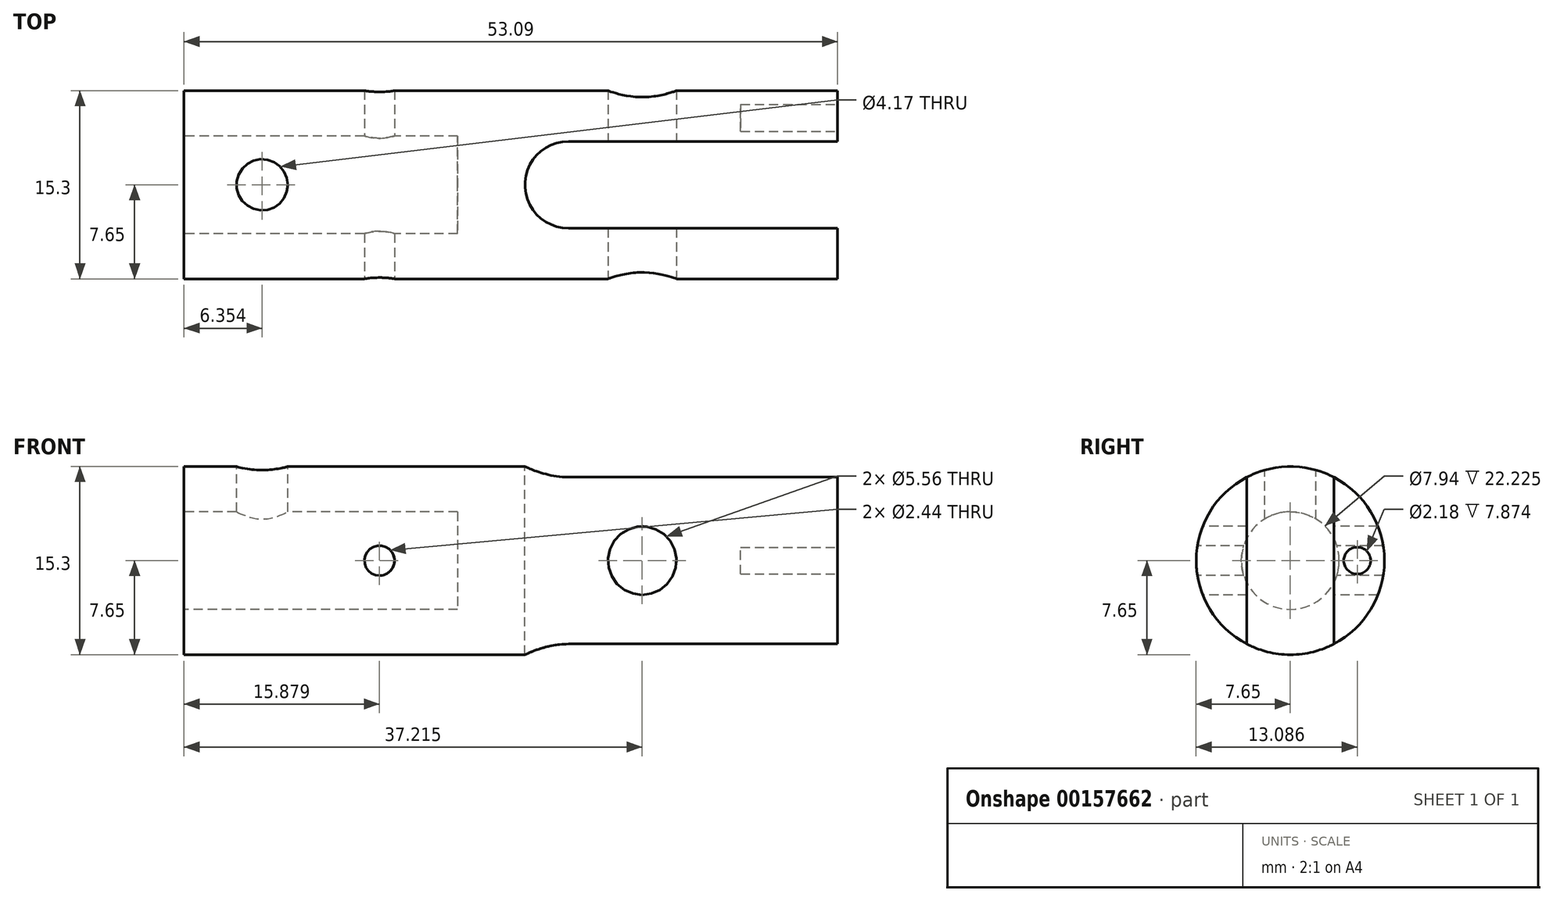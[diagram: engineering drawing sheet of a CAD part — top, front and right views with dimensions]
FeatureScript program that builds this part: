
annotation { "Feature Type Name" : "Feature", "Feature Type Description" : "" }
export const myFeature = defineFeature(function(context is Context, id is Id, definition is map)
    precondition{}
    {
        {
            var Q0;
            Q0=qCreatedBy(makeId("Right.planeOp"),FACE);
            var sketch = newSketch(context, id + "F0", { "sketchPlane" : qUnion([Q0])});
            skCircle(sketch, "E0", {"center": v(0, 0) * mm, "radius": 7.65 * mm});
            skSolve(sketch);
        }
        {
            var Q0;
            Q0=makeQuery(id+"F0.imprint","IMPRINT",FACE,{"disambiguationData":[TD([[makeQuery(id+"F0.imprint","IMPRINT",EDGE,{"derivedFrom":sQuery(id+"F0.wireOp",EDGE,"E0")}),1.0]])]});
            extrude(context, id + "F1", {"entities" : qUnion([Q0]), "oppositeDirection" : true, "depth" : 53.1 * mm});
        }
        {
            var Q0;
            Q0=qCreatedBy(makeId("Top.planeOp"),FACE);
            cPlane(context, id + "F2", {"entities" : qUnion([Q0]), "cplaneType" : CPlaneType.OFFSET, "offset" : 7.87 * mm, "width" : 152.4 * mm, "height" : 152.4 * mm});
        }
        {
            var Q0;
            Q0=qCreatedBy(id+"F2.planeOp",FACE);
            var sketch = newSketch(context, id + "F3", { "sketchPlane" : qUnion([Q0])});
            skLineSegment(sketch, "E1.bottom", {"start": v(-21.87, 3.53) * mm, "end": v(25.4, 3.53) * mm});
            skLineSegment(sketch, "E1.top", {"start": v(-21.87, -3.53) * mm, "end": v(25.4, -3.53) * mm});
            skLineSegment(sketch, "E1.left", {"start": v(-25.4, 0) * mm, "end": v(-25.4, 0) * mm});
            skLineSegment(sketch, "E1.right", {"start": v(25.4, 3.53) * mm, "end": v(25.4, -3.53) * mm});
            skPoint(sketch, "E1.middle", {"position": v(0, 0) * mm});
            skPoint(sketch, "E2.visualSharp", {"position": v(-25.4, 3.53) * mm});
            skArc(sketch, "E2.filletArc", {"start": v(-21.87, 3.53) * mm, "mid": v(-24.37, 2.5) * mm, "end": v(-25.4, 0) * mm});
            skPoint(sketch, "E3.visualSharp", {"position": v(-25.4, -3.53) * mm});
            skArc(sketch, "E3.filletArc", {"start": v(-25.4, 0) * mm, "mid": v(-24.37, -2.5) * mm, "end": v(-21.87, -3.53) * mm});
            skSolve(sketch);
        }
        {
            var Q0;
            Q0=makeQuery(id+"F3.imprint","IMPRINT",FACE,{"disambiguationData":[TD([[makeQuery(id+"F3.imprint","IMPRINT",EDGE,{"derivedFrom":sQuery(id+"F3.wireOp",EDGE,"E1.bottom")}),-1.0]])]});
            extrude(context, id + "F4", {"entities" : qUnion([Q0]), "operationType" : NewBodyOperationType.REMOVE, "endBound" : BoundingType.THROUGH_ALL, "oppositeDirection" : true, "depth" : 25.4 * mm});
        }
        {
            var Q0;
            Q0=makeQuery(id+"F1.opExtrude","CAP_FACE",FACE,{"disambiguationData":[OSD([sQuery(id+"F0.wireOp",EDGE,"E0")])],"isStart":false});
            var sketch = newSketch(context, id + "F5", { "sketchPlane" : qUnion([Q0])});
            skCircle(sketch, "E4", {"center": v(0, 0) * mm, "radius": 3.97 * mm});
            skSolve(sketch);
        }
        {
            var Q0;
            Q0=makeQuery(id+"F5.imprint","IMPRINT",FACE,{"disambiguationData":[TD([[makeQuery(id+"F5.imprint","IMPRINT",EDGE,{"derivedFrom":sQuery(id+"F5.wireOp",EDGE,"E4")}),1.0]])]});
            extrude(context, id + "F6", {"entities" : qUnion([Q0]), "operationType" : NewBodyOperationType.REMOVE, "oppositeDirection" : true, "depth" : 22.22 * mm});
        }
        {
            var Q0;
            Q0=qCreatedBy(id+"F2.planeOp",FACE);
            var sketch = newSketch(context, id + "F7", { "sketchPlane" : qUnion([Q0])});
            skCircle(sketch, "E5", {"center": v(-46.74, 0) * mm, "radius": 2.08 * mm});
            skSolve(sketch);
        }
        {
            var Q0;
            Q0=makeQuery(id+"F7.imprint","IMPRINT",FACE,{"disambiguationData":[TD([[makeQuery(id+"F7.imprint","IMPRINT",EDGE,{"derivedFrom":sQuery(id+"F7.wireOp",EDGE,"E5")}),1.0]])]});
            extrude(context, id + "F8", {"entities" : qUnion([Q0]), "operationType" : NewBodyOperationType.REMOVE, "oppositeDirection" : true, "depth" : 7.62 * mm});
        }
        {
            var Q0;
            {var subQ0=sQuery(id+"F0.wireOp",EDGE,"E0");Q0=makeQuery(id+"F4.boolean.opBoolean","SPLIT",FACE,{"disambiguationData":[TD([makeQuery(id+"F4.opExtrude","SWEPT_FACE",FACE,{"disambiguationData":[OSD([sQuery(id+"F3.wireOp",EDGE,"E1.bottom")])]})])],"derivedFrom":makeQuery(id+"F1.opExtrude","CAP_FACE",FACE,{"disambiguationData":[OSD([subQ0])],"isStart":true})});}
            var sketch = newSketch(context, id + "F9", { "sketchPlane" : qUnion([Q0])});
            skCircle(sketch, "E6", {"center": v(5.44, 0) * mm, "radius": 1.1 * mm});
            skSolve(sketch);
        }
        {
            var Q0;
            Q0=makeQuery(id+"F9.imprint","IMPRINT",FACE,{"disambiguationData":[TD([[makeQuery(id+"F9.imprint","IMPRINT",EDGE,{"derivedFrom":sQuery(id+"F9.wireOp",EDGE,"E6")}),1.0]])]});
            extrude(context, id + "F10", {"entities" : qUnion([Q0]), "operationType" : NewBodyOperationType.REMOVE, "oppositeDirection" : true, "depth" : 7.87 * mm});
        }
        {
            var Q0;
            Q0=qCreatedBy(makeId("Front.planeOp"),FACE);
            cPlane(context, id + "F11", {"entities" : qUnion([Q0]), "cplaneType" : CPlaneType.OFFSET, "offset" : 7.87 * mm, "width" : 152.4 * mm, "height" : 152.4 * mm});
        }
        {
            var Q0;
            Q0=qCreatedBy(id+"F11.planeOp",FACE);
            var sketch = newSketch(context, id + "F12", { "sketchPlane" : qUnion([Q0])});
            skCircle(sketch, "E7", {"center": v(-15.88, 0) * mm, "radius": 2.78 * mm});
            skSolve(sketch);
        }
        {
            var Q0;
            Q0=makeQuery(id+"F12.imprint","IMPRINT",FACE,{"disambiguationData":[TD([[makeQuery(id+"F12.imprint","IMPRINT",EDGE,{"derivedFrom":sQuery(id+"F12.wireOp",EDGE,"E7")}),1.0]])]});
            extrude(context, id + "F13", {"entities" : qUnion([Q0]), "operationType" : NewBodyOperationType.REMOVE, "endBound" : BoundingType.THROUGH_ALL, "oppositeDirection" : true, "depth" : 25.4 * mm});
        }
        {
            var Q0;
            Q0=qCreatedBy(id+"F11.planeOp",FACE);
            var sketch = newSketch(context, id + "F14", { "sketchPlane" : qUnion([Q0])});
            skCircle(sketch, "E8", {"center": v(-37.21, 0) * mm, "radius": 1.22 * mm});
            skSolve(sketch);
        }
        {
            var Q0;
            Q0=makeQuery(id+"F14.imprint","IMPRINT",FACE,{"disambiguationData":[TD([[makeQuery(id+"F14.imprint","IMPRINT",EDGE,{"derivedFrom":sQuery(id+"F14.wireOp",EDGE,"E8")}),1.0]])]});
            extrude(context, id + "F15", {"entities" : qUnion([Q0]), "operationType" : NewBodyOperationType.REMOVE, "endBound" : BoundingType.THROUGH_ALL, "oppositeDirection" : true, "depth" : 25.4 * mm});
        }
    });
